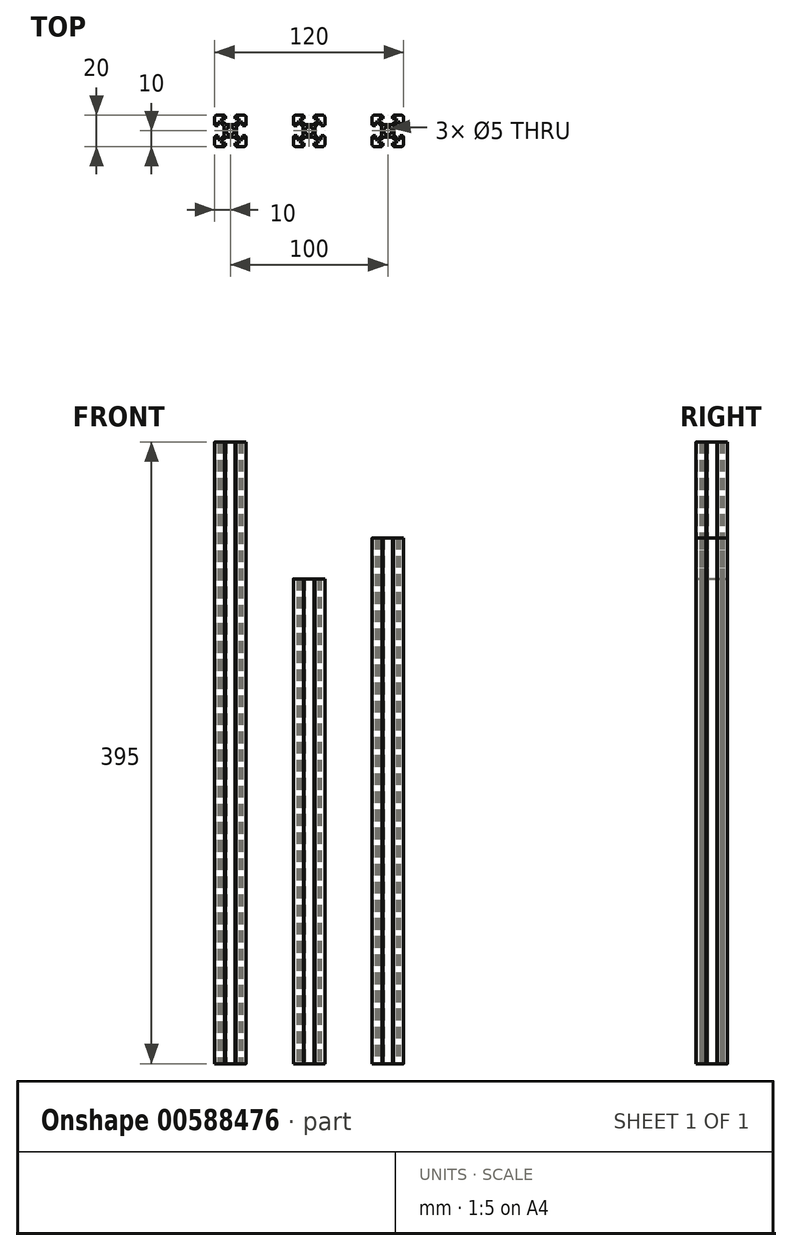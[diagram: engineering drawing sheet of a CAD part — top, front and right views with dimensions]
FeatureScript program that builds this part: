
annotation { "Feature Type Name" : "Feature", "Feature Type Description" : "" }
export const myFeature = defineFeature(function(context is Context, id is Id, definition is map)
    precondition{}
    {
        {
            var Q0;
            Q0=qCreatedBy(makeId("Top.planeOp"),FACE);
            var sketch = newSketch(context, id + "F0", { "sketchPlane" : qUnion([Q0])});
            skLineSegment(sketch, "E0", {"start": v(-2.5, 0) * mm, "end": v(-3.9, 0) * mm});
            skLineSegment(sketch, "E1", {"start": v(-3.9, 0) * mm, "end": v(-3.9, 2.05) * mm});
            skLineSegment(sketch, "E2", {"start": v(-4.49, 3.46) * mm, "end": v(-6.6, 5.58) * mm});
            skLineSegment(sketch, "E3", {"start": v(-6.6, 5.58) * mm, "end": v(-7.7, 5.58) * mm});
            skLineSegment(sketch, "E4", {"start": v(-7.7, 5.58) * mm, "end": v(-7.7, 3.18) * mm});
            skLineSegment(sketch, "E5", {"start": v(-7.7, 3.18) * mm, "end": v(-9.5, 3.18) * mm});
            skLineSegment(sketch, "E6", {"start": v(-9.5, 3.18) * mm, "end": v(-9.5, 3.68) * mm});
            skLineSegment(sketch, "E7", {"start": v(-9.5, 3.68) * mm, "end": v(-10, 3.68) * mm});
            skLineSegment(sketch, "E8", {"start": v(-10, 3.68) * mm, "end": v(-10, 8.5) * mm});
            skLineSegment(sketch, "E9", {"start": v(-8.5, 10) * mm, "end": v(-3.6, 10) * mm});
            skLineSegment(sketch, "E10", {"start": v(-3.6, 10) * mm, "end": v(-3.6, 9.5) * mm});
            skLineSegment(sketch, "E11", {"start": v(-3.6, 9.5) * mm, "end": v(-3.1, 9.5) * mm});
            skLineSegment(sketch, "E12", {"start": v(-3.1, 9.5) * mm, "end": v(-3.1, 7.7) * mm});
            skLineSegment(sketch, "E13", {"start": v(-3.1, 7.7) * mm, "end": v(-5.5, 7.7) * mm});
            skLineSegment(sketch, "E14", {"start": v(-5.5, 7.7) * mm, "end": v(-5.5, 6.6) * mm});
            skLineSegment(sketch, "E15", {"start": v(-5.5, 6.6) * mm, "end": v(-3.39, 4.49) * mm});
            skLineSegment(sketch, "E16", {"start": v(-1.97, 3.9) * mm, "end": v(0, 3.9) * mm});
            skLineSegment(sketch, "E17", {"start": v(0, 3.9) * mm, "end": v(0, 20.22) * mm, "construction": true});
            skLineSegment(sketch, "E18", {"start": v(-3.9, 0) * mm, "end": v(-20.4, 0) * mm, "construction": true});
            skPoint(sketch, "E19.visualSharp", {"position": v(-10, 10) * mm});
            skArc(sketch, "E19.filletArc", {"start": v(-8.5, 10) * mm, "mid": v(-9.56, 9.56) * mm, "end": v(-10, 8.5) * mm});
            skPoint(sketch, "E20.visualSharp", {"position": v(-2.8, 3.9) * mm});
            skArc(sketch, "E20.filletArc", {"start": v(-3.39, 4.49) * mm, "mid": v(-2.74, 4.05) * mm, "end": v(-1.97, 3.9) * mm});
            skPoint(sketch, "E21.visualSharp", {"position": v(-3.9, 2.88) * mm});
            skArc(sketch, "E21.filletArc", {"start": v(-3.9, 2.05) * mm, "mid": v(-4.05, 2.82) * mm, "end": v(-4.49, 3.46) * mm});
            skLineSegment(sketch, "E22", {"start": v(0, 3.9) * mm, "end": v(0, 2.5) * mm});
            skArc(sketch, "E23", {"start": v(-2.5, 0) * mm, "mid": v(-1.77, 1.77) * mm, "end": v(0, 2.5) * mm});
            skLineSegment(sketch, "E24.MirrorCS", {"start": v(9.5, 3.68) * mm, "end": v(10, 3.68) * mm});
            skLineSegment(sketch, "E25.MirrorCS", {"start": v(2.5, 0) * mm, "end": v(3.9, 0) * mm});
            skLineSegment(sketch, "E26.MirrorCS", {"start": v(9.5, 3.18) * mm, "end": v(9.5, 3.68) * mm});
            skArc(sketch, "E27.MirrorCS", {"start": v(3.9, 2.05) * mm, "mid": v(4.05, 2.82) * mm, "end": v(4.49, 3.46) * mm});
            skLineSegment(sketch, "E28.MirrorCS", {"start": v(3.6, 10) * mm, "end": v(3.6, 9.5) * mm});
            skLineSegment(sketch, "E29.MirrorCS", {"start": v(6.6, 5.58) * mm, "end": v(7.7, 5.58) * mm});
            skLineSegment(sketch, "E30.MirrorCS", {"start": v(3.6, 9.5) * mm, "end": v(3.1, 9.5) * mm});
            skLineSegment(sketch, "E31.MirrorCS", {"start": v(5.5, 6.6) * mm, "end": v(3.39, 4.49) * mm});
            skLineSegment(sketch, "E32.MirrorCS", {"start": v(5.5, 7.7) * mm, "end": v(5.5, 6.6) * mm});
            skArc(sketch, "E33.MirrorCS", {"start": v(8.5, 10) * mm, "mid": v(9.56, 9.56) * mm, "end": v(10, 8.5) * mm});
            skLineSegment(sketch, "E34.MirrorCS", {"start": v(3.9, 0) * mm, "end": v(3.9, 2.05) * mm});
            skLineSegment(sketch, "E35.MirrorCS", {"start": v(7.7, 5.58) * mm, "end": v(7.7, 3.18) * mm});
            skLineSegment(sketch, "E36.MirrorCS", {"start": v(7.7, 3.18) * mm, "end": v(9.5, 3.18) * mm});
            skLineSegment(sketch, "E37.MirrorCS", {"start": v(3.1, 7.7) * mm, "end": v(5.5, 7.7) * mm});
            skLineSegment(sketch, "E38.MirrorCS", {"start": v(1.97, 3.9) * mm, "end": v(0, 3.9) * mm});
            skArc(sketch, "E39.MirrorCS", {"start": v(3.39, 4.49) * mm, "mid": v(2.74, 4.05) * mm, "end": v(1.97, 3.9) * mm});
            skLineSegment(sketch, "E40.MirrorCS", {"start": v(3.1, 9.5) * mm, "end": v(3.1, 7.7) * mm});
            skArc(sketch, "E41.MirrorCS", {"start": v(2.5, 0) * mm, "mid": v(1.77, 1.77) * mm, "end": v(0, 2.5) * mm});
            skLineSegment(sketch, "E42.MirrorCS", {"start": v(4.49, 3.46) * mm, "end": v(6.6, 5.58) * mm});
            skLineSegment(sketch, "E43.MirrorCS", {"start": v(8.5, 10) * mm, "end": v(3.6, 10) * mm});
            skPoint(sketch, "E44.MirrorP", {"position": v(3.9, 2.88) * mm});
            skPoint(sketch, "E45.MirrorP", {"position": v(2.8, 3.9) * mm});
            skPoint(sketch, "E46.MirrorP", {"position": v(10, 10) * mm});
            skLineSegment(sketch, "E47.MirrorCS", {"start": v(10, 3.68) * mm, "end": v(10, 8.5) * mm});
            skLineSegment(sketch, "E48.MirrorCS", {"start": v(0, -3.9) * mm, "end": v(0, -2.5) * mm});
            skLineSegment(sketch, "E49.MirrorCS", {"start": v(-9.5, -3.68) * mm, "end": v(-10, -3.68) * mm});
            skLineSegment(sketch, "E50.MirrorCS", {"start": v(-9.5, -3.18) * mm, "end": v(-9.5, -3.68) * mm});
            skLineSegment(sketch, "E51.MirrorCS", {"start": v(-5.5, -7.7) * mm, "end": v(-5.5, -6.6) * mm});
            skLineSegment(sketch, "E52.MirrorCS", {"start": v(3.6, -9.5) * mm, "end": v(3.1, -9.5) * mm});
            skLineSegment(sketch, "E53.MirrorCS", {"start": v(3.6, -10) * mm, "end": v(3.6, -9.5) * mm});
            skLineSegment(sketch, "E54.MirrorCS", {"start": v(-3.9, 0) * mm, "end": v(-3.9, -2.05) * mm});
            skLineSegment(sketch, "E55.MirrorCS", {"start": v(9.5, -3.18) * mm, "end": v(9.5, -3.68) * mm});
            skLineSegment(sketch, "E56.MirrorCS", {"start": v(-5.5, -6.6) * mm, "end": v(-3.39, -4.49) * mm});
            skLineSegment(sketch, "E57.MirrorCS", {"start": v(-6.6, -5.58) * mm, "end": v(-7.7, -5.58) * mm});
            skLineSegment(sketch, "E58.MirrorCS", {"start": v(-4.49, -3.46) * mm, "end": v(-6.6, -5.58) * mm});
            skArc(sketch, "E59.MirrorCS", {"start": v(3.9, -2.05) * mm, "mid": v(4.05, -2.82) * mm, "end": v(4.49, -3.46) * mm});
            skArc(sketch, "E60.MirrorCS", {"start": v(-3.9, -2.05) * mm, "mid": v(-4.05, -2.82) * mm, "end": v(-4.49, -3.46) * mm});
            skLineSegment(sketch, "E61.MirrorCS", {"start": v(3.9, 0) * mm, "end": v(3.9, -2.05) * mm});
            skLineSegment(sketch, "E62.MirrorCS", {"start": v(-3.1, -7.7) * mm, "end": v(-5.5, -7.7) * mm});
            skLineSegment(sketch, "E63.MirrorCS", {"start": v(1.97, -3.9) * mm, "end": v(0, -3.9) * mm});
            skLineSegment(sketch, "E64.MirrorCS", {"start": v(9.5, -3.68) * mm, "end": v(10, -3.68) * mm});
            skLineSegment(sketch, "E65.MirrorCS", {"start": v(7.7, -5.58) * mm, "end": v(7.7, -3.18) * mm});
            skLineSegment(sketch, "E66.MirrorCS", {"start": v(3.1, -9.5) * mm, "end": v(3.1, -7.7) * mm});
            skLineSegment(sketch, "E67.MirrorCS", {"start": v(6.6, -5.58) * mm, "end": v(7.7, -5.58) * mm});
            skLineSegment(sketch, "E68.MirrorCS", {"start": v(7.7, -3.18) * mm, "end": v(9.5, -3.18) * mm});
            skLineSegment(sketch, "E69.MirrorCS", {"start": v(3.1, -7.7) * mm, "end": v(5.5, -7.7) * mm});
            skArc(sketch, "E70.MirrorCS", {"start": v(3.39, -4.49) * mm, "mid": v(2.74, -4.05) * mm, "end": v(1.97, -3.9) * mm});
            skLineSegment(sketch, "E71.MirrorCS", {"start": v(-7.7, -5.58) * mm, "end": v(-7.7, -3.18) * mm});
            skArc(sketch, "E72.MirrorCS", {"start": v(-3.39, -4.49) * mm, "mid": v(-2.74, -4.05) * mm, "end": v(-1.97, -3.9) * mm});
            skLineSegment(sketch, "E73.MirrorCS", {"start": v(-3.1, -9.5) * mm, "end": v(-3.1, -7.7) * mm});
            skLineSegment(sketch, "E74.MirrorCS", {"start": v(5.5, -6.6) * mm, "end": v(3.39, -4.49) * mm});
            skLineSegment(sketch, "E75.MirrorCS", {"start": v(-3.6, -9.5) * mm, "end": v(-3.1, -9.5) * mm});
            skLineSegment(sketch, "E76.MirrorCS", {"start": v(-7.7, -3.18) * mm, "end": v(-9.5, -3.18) * mm});
            skLineSegment(sketch, "E77.MirrorCS", {"start": v(-3.6, -10) * mm, "end": v(-3.6, -9.5) * mm});
            skLineSegment(sketch, "E78.MirrorCS", {"start": v(-1.97, -3.9) * mm, "end": v(0, -3.9) * mm});
            skLineSegment(sketch, "E79.MirrorCS", {"start": v(5.5, -7.7) * mm, "end": v(5.5, -6.6) * mm});
            skArc(sketch, "E80.MirrorCS", {"start": v(8.5, -10) * mm, "mid": v(9.56, -9.56) * mm, "end": v(10, -8.5) * mm});
            skArc(sketch, "E81.MirrorCS", {"start": v(-2.5, 0) * mm, "mid": v(-1.77, -1.77) * mm, "end": v(0, -2.5) * mm});
            skArc(sketch, "E82.MirrorCS", {"start": v(-8.5, -10) * mm, "mid": v(-9.56, -9.56) * mm, "end": v(-10, -8.5) * mm});
            skLineSegment(sketch, "E83.MirrorCS", {"start": v(-8.5, -10) * mm, "end": v(-3.6, -10) * mm});
            skLineSegment(sketch, "E84.MirrorCS", {"start": v(8.5, -10) * mm, "end": v(3.6, -10) * mm});
            skLineSegment(sketch, "E85.MirrorCS", {"start": v(0, -3.9) * mm, "end": v(0, -20.22) * mm, "construction": true});
            skLineSegment(sketch, "E86.MirrorCS", {"start": v(10, -3.68) * mm, "end": v(10, -8.5) * mm});
            skLineSegment(sketch, "E87.MirrorCS", {"start": v(-10, -3.68) * mm, "end": v(-10, -8.5) * mm});
            skLineSegment(sketch, "E88.MirrorCS", {"start": v(4.49, -3.46) * mm, "end": v(6.6, -5.58) * mm});
            skPoint(sketch, "E89.MirrorP", {"position": v(10, -10) * mm});
            skPoint(sketch, "E90.MirrorP", {"position": v(-3.9, -2.88) * mm});
            skArc(sketch, "E91.MirrorCS", {"start": v(2.5, 0) * mm, "mid": v(1.77, -1.77) * mm, "end": v(0, -2.5) * mm});
            skPoint(sketch, "E92.MirrorP", {"position": v(-2.8, -3.9) * mm});
            skPoint(sketch, "E93.MirrorP", {"position": v(-10, -10) * mm});
            skPoint(sketch, "E94.MirrorP", {"position": v(3.9, -2.88) * mm});
            skPoint(sketch, "E95.MirrorP", {"position": v(2.8, -3.9) * mm});
            skSolve(sketch);
        }
        {
            var Q0;
            Q0 = qSketchRegion(id + "F0", true);
            extrude(context, id + "F1", {"entities" : qUnion([Q0]), "depth" : 334 * mm, "offsetDistance" : 25 * mm});
        }
        {
            var Q0;
            Q0=makeQuery(id+"F1.opExtrude","SWEPT_BODY",BODY,{"disambiguationData":[OSD([sQuery(id+"F0.wireOp",EDGE,"E1"),sQuery(id+"F0.wireOp",EDGE,"E2"),sQuery(id+"F0.wireOp",EDGE,"E3"),sQuery(id+"F0.wireOp",EDGE,"E4"),sQuery(id+"F0.wireOp",EDGE,"E5"),sQuery(id+"F0.wireOp",EDGE,"E6"),sQuery(id+"F0.wireOp",EDGE,"E7"),sQuery(id+"F0.wireOp",EDGE,"E8"),sQuery(id+"F0.wireOp",EDGE,"E9"),sQuery(id+"F0.wireOp",EDGE,"E10"),sQuery(id+"F0.wireOp",EDGE,"E11"),sQuery(id+"F0.wireOp",EDGE,"E12"),sQuery(id+"F0.wireOp",EDGE,"E13"),sQuery(id+"F0.wireOp",EDGE,"E14"),sQuery(id+"F0.wireOp",EDGE,"E15"),sQuery(id+"F0.wireOp",EDGE,"E16"),sQuery(id+"F0.wireOp",EDGE,"E19.filletArc"),sQuery(id+"F0.wireOp",EDGE,"E20.filletArc"),sQuery(id+"F0.wireOp",EDGE,"E21.filletArc"),sQuery(id+"F0.wireOp",EDGE,"E23"),sQuery(id+"F0.wireOp",EDGE,"E24.MirrorCS"),sQuery(id+"F0.wireOp",EDGE,"E26.MirrorCS"),sQuery(id+"F0.wireOp",EDGE,"E27.MirrorCS"),sQuery(id+"F0.wireOp",EDGE,"E28.MirrorCS"),sQuery(id+"F0.wireOp",EDGE,"E29.MirrorCS"),sQuery(id+"F0.wireOp",EDGE,"E30.MirrorCS"),sQuery(id+"F0.wireOp",EDGE,"E31.MirrorCS"),sQuery(id+"F0.wireOp",EDGE,"E32.MirrorCS"),sQuery(id+"F0.wireOp",EDGE,"E33.MirrorCS"),sQuery(id+"F0.wireOp",EDGE,"E34.MirrorCS"),sQuery(id+"F0.wireOp",EDGE,"E35.MirrorCS"),sQuery(id+"F0.wireOp",EDGE,"E36.MirrorCS"),sQuery(id+"F0.wireOp",EDGE,"E37.MirrorCS"),sQuery(id+"F0.wireOp",EDGE,"E38.MirrorCS"),sQuery(id+"F0.wireOp",EDGE,"E39.MirrorCS"),sQuery(id+"F0.wireOp",EDGE,"E40.MirrorCS"),sQuery(id+"F0.wireOp",EDGE,"E41.MirrorCS"),sQuery(id+"F0.wireOp",EDGE,"E42.MirrorCS"),sQuery(id+"F0.wireOp",EDGE,"E43.MirrorCS"),sQuery(id+"F0.wireOp",EDGE,"E47.MirrorCS"),sQuery(id+"F0.wireOp",EDGE,"E49.MirrorCS"),sQuery(id+"F0.wireOp",EDGE,"E50.MirrorCS"),sQuery(id+"F0.wireOp",EDGE,"E51.MirrorCS"),sQuery(id+"F0.wireOp",EDGE,"E52.MirrorCS"),sQuery(id+"F0.wireOp",EDGE,"E53.MirrorCS"),sQuery(id+"F0.wireOp",EDGE,"E54.MirrorCS"),sQuery(id+"F0.wireOp",EDGE,"E55.MirrorCS"),sQuery(id+"F0.wireOp",EDGE,"E56.MirrorCS"),sQuery(id+"F0.wireOp",EDGE,"E57.MirrorCS"),sQuery(id+"F0.wireOp",EDGE,"E58.MirrorCS"),sQuery(id+"F0.wireOp",EDGE,"E59.MirrorCS"),sQuery(id+"F0.wireOp",EDGE,"E60.MirrorCS"),sQuery(id+"F0.wireOp",EDGE,"E61.MirrorCS"),sQuery(id+"F0.wireOp",EDGE,"E62.MirrorCS"),sQuery(id+"F0.wireOp",EDGE,"E63.MirrorCS"),sQuery(id+"F0.wireOp",EDGE,"E64.MirrorCS"),sQuery(id+"F0.wireOp",EDGE,"E65.MirrorCS"),sQuery(id+"F0.wireOp",EDGE,"E66.MirrorCS"),sQuery(id+"F0.wireOp",EDGE,"E67.MirrorCS"),sQuery(id+"F0.wireOp",EDGE,"E68.MirrorCS"),sQuery(id+"F0.wireOp",EDGE,"E69.MirrorCS"),sQuery(id+"F0.wireOp",EDGE,"E70.MirrorCS"),sQuery(id+"F0.wireOp",EDGE,"E71.MirrorCS"),sQuery(id+"F0.wireOp",EDGE,"E72.MirrorCS"),sQuery(id+"F0.wireOp",EDGE,"E73.MirrorCS"),sQuery(id+"F0.wireOp",EDGE,"E74.MirrorCS"),sQuery(id+"F0.wireOp",EDGE,"E75.MirrorCS"),sQuery(id+"F0.wireOp",EDGE,"E76.MirrorCS"),sQuery(id+"F0.wireOp",EDGE,"E77.MirrorCS"),sQuery(id+"F0.wireOp",EDGE,"E78.MirrorCS"),sQuery(id+"F0.wireOp",EDGE,"E79.MirrorCS"),sQuery(id+"F0.wireOp",EDGE,"E80.MirrorCS"),sQuery(id+"F0.wireOp",EDGE,"E81.MirrorCS"),sQuery(id+"F0.wireOp",EDGE,"E82.MirrorCS"),sQuery(id+"F0.wireOp",EDGE,"E83.MirrorCS"),sQuery(id+"F0.wireOp",EDGE,"E84.MirrorCS"),sQuery(id+"F0.wireOp",EDGE,"E86.MirrorCS"),sQuery(id+"F0.wireOp",EDGE,"E87.MirrorCS"),sQuery(id+"F0.wireOp",EDGE,"E88.MirrorCS"),sQuery(id+"F0.wireOp",EDGE,"E91.MirrorCS")])]});
            transform(context, id + "F2", {"entities" : qUnion([Q0]), "transformType" : TransformType.TRANSLATION_3D, "dx" : 100 * mm, "dy" : 0 * mm, "dz" : 0 * mm, "makeCopy" : false});
        }
        {
            var Q0;
            Q0=makeQuery(id+"F0.imprint","IMPRINT",FACE,{"disambiguationData":[TD([[makeQuery(id+"F0.imprint","IMPRINT",EDGE,{"derivedFrom":sQuery(id+"F0.wireOp",EDGE,"E48.MirrorCS")}),1.0]])]});
            var Q1;
            Q1=makeQuery(id+"F0.imprint","IMPRINT",FACE,{"disambiguationData":[TD([[makeQuery(id+"F0.imprint","IMPRINT",EDGE,{"derivedFrom":sQuery(id+"F0.wireOp",EDGE,"E1")}),-1.0]])]});
            var Q2;
            Q2=makeQuery(id+"F0.imprint","IMPRINT",FACE,{"disambiguationData":[TD([[makeQuery(id+"F0.imprint","IMPRINT",EDGE,{"derivedFrom":sQuery(id+"F0.wireOp",EDGE,"E24.MirrorCS")}),1.0]])]});
            var Q3;
            Q3=makeQuery(id+"F0.imprint","IMPRINT",FACE,{"disambiguationData":[TD([[makeQuery(id+"F0.imprint","IMPRINT",EDGE,{"derivedFrom":sQuery(id+"F0.wireOp",EDGE,"E48.MirrorCS")}),-1.0]])]});
            extrude(context, id + "F3", {"entities" : qUnion([Q0, Q1, Q2, Q3]), "depth" : 308 * mm, "offsetDistance" : 25 * mm});
        }
        {
            var Q0;
            Q0=makeQuery(id+"F3.opExtrude","SWEPT_BODY",BODY,{"disambiguationData":[OSD([sQuery(id+"F0.wireOp",EDGE,"E1"),sQuery(id+"F0.wireOp",EDGE,"E2"),sQuery(id+"F0.wireOp",EDGE,"E3"),sQuery(id+"F0.wireOp",EDGE,"E4"),sQuery(id+"F0.wireOp",EDGE,"E5"),sQuery(id+"F0.wireOp",EDGE,"E6"),sQuery(id+"F0.wireOp",EDGE,"E7"),sQuery(id+"F0.wireOp",EDGE,"E8"),sQuery(id+"F0.wireOp",EDGE,"E9"),sQuery(id+"F0.wireOp",EDGE,"E10"),sQuery(id+"F0.wireOp",EDGE,"E11"),sQuery(id+"F0.wireOp",EDGE,"E12"),sQuery(id+"F0.wireOp",EDGE,"E13"),sQuery(id+"F0.wireOp",EDGE,"E14"),sQuery(id+"F0.wireOp",EDGE,"E15"),sQuery(id+"F0.wireOp",EDGE,"E16"),sQuery(id+"F0.wireOp",EDGE,"E19.filletArc"),sQuery(id+"F0.wireOp",EDGE,"E20.filletArc"),sQuery(id+"F0.wireOp",EDGE,"E21.filletArc"),sQuery(id+"F0.wireOp",EDGE,"E23"),sQuery(id+"F0.wireOp",EDGE,"E24.MirrorCS"),sQuery(id+"F0.wireOp",EDGE,"E26.MirrorCS"),sQuery(id+"F0.wireOp",EDGE,"E27.MirrorCS"),sQuery(id+"F0.wireOp",EDGE,"E28.MirrorCS"),sQuery(id+"F0.wireOp",EDGE,"E29.MirrorCS"),sQuery(id+"F0.wireOp",EDGE,"E30.MirrorCS"),sQuery(id+"F0.wireOp",EDGE,"E31.MirrorCS"),sQuery(id+"F0.wireOp",EDGE,"E32.MirrorCS"),sQuery(id+"F0.wireOp",EDGE,"E33.MirrorCS"),sQuery(id+"F0.wireOp",EDGE,"E34.MirrorCS"),sQuery(id+"F0.wireOp",EDGE,"E35.MirrorCS"),sQuery(id+"F0.wireOp",EDGE,"E36.MirrorCS"),sQuery(id+"F0.wireOp",EDGE,"E37.MirrorCS"),sQuery(id+"F0.wireOp",EDGE,"E38.MirrorCS"),sQuery(id+"F0.wireOp",EDGE,"E39.MirrorCS"),sQuery(id+"F0.wireOp",EDGE,"E40.MirrorCS"),sQuery(id+"F0.wireOp",EDGE,"E41.MirrorCS"),sQuery(id+"F0.wireOp",EDGE,"E42.MirrorCS"),sQuery(id+"F0.wireOp",EDGE,"E43.MirrorCS"),sQuery(id+"F0.wireOp",EDGE,"E47.MirrorCS"),sQuery(id+"F0.wireOp",EDGE,"E49.MirrorCS"),sQuery(id+"F0.wireOp",EDGE,"E50.MirrorCS"),sQuery(id+"F0.wireOp",EDGE,"E51.MirrorCS"),sQuery(id+"F0.wireOp",EDGE,"E52.MirrorCS"),sQuery(id+"F0.wireOp",EDGE,"E53.MirrorCS"),sQuery(id+"F0.wireOp",EDGE,"E54.MirrorCS"),sQuery(id+"F0.wireOp",EDGE,"E55.MirrorCS"),sQuery(id+"F0.wireOp",EDGE,"E56.MirrorCS"),sQuery(id+"F0.wireOp",EDGE,"E57.MirrorCS"),sQuery(id+"F0.wireOp",EDGE,"E58.MirrorCS"),sQuery(id+"F0.wireOp",EDGE,"E59.MirrorCS"),sQuery(id+"F0.wireOp",EDGE,"E60.MirrorCS"),sQuery(id+"F0.wireOp",EDGE,"E61.MirrorCS"),sQuery(id+"F0.wireOp",EDGE,"E62.MirrorCS"),sQuery(id+"F0.wireOp",EDGE,"E63.MirrorCS"),sQuery(id+"F0.wireOp",EDGE,"E64.MirrorCS"),sQuery(id+"F0.wireOp",EDGE,"E65.MirrorCS"),sQuery(id+"F0.wireOp",EDGE,"E66.MirrorCS"),sQuery(id+"F0.wireOp",EDGE,"E67.MirrorCS"),sQuery(id+"F0.wireOp",EDGE,"E68.MirrorCS"),sQuery(id+"F0.wireOp",EDGE,"E69.MirrorCS"),sQuery(id+"F0.wireOp",EDGE,"E70.MirrorCS"),sQuery(id+"F0.wireOp",EDGE,"E71.MirrorCS"),sQuery(id+"F0.wireOp",EDGE,"E72.MirrorCS"),sQuery(id+"F0.wireOp",EDGE,"E73.MirrorCS"),sQuery(id+"F0.wireOp",EDGE,"E74.MirrorCS"),sQuery(id+"F0.wireOp",EDGE,"E75.MirrorCS"),sQuery(id+"F0.wireOp",EDGE,"E76.MirrorCS"),sQuery(id+"F0.wireOp",EDGE,"E77.MirrorCS"),sQuery(id+"F0.wireOp",EDGE,"E78.MirrorCS"),sQuery(id+"F0.wireOp",EDGE,"E79.MirrorCS"),sQuery(id+"F0.wireOp",EDGE,"E80.MirrorCS"),sQuery(id+"F0.wireOp",EDGE,"E81.MirrorCS"),sQuery(id+"F0.wireOp",EDGE,"E82.MirrorCS"),sQuery(id+"F0.wireOp",EDGE,"E83.MirrorCS"),sQuery(id+"F0.wireOp",EDGE,"E84.MirrorCS"),sQuery(id+"F0.wireOp",EDGE,"E86.MirrorCS"),sQuery(id+"F0.wireOp",EDGE,"E87.MirrorCS"),sQuery(id+"F0.wireOp",EDGE,"E88.MirrorCS"),sQuery(id+"F0.wireOp",EDGE,"E91.MirrorCS")])]});
            transform(context, id + "F4", {"entities" : qUnion([Q0]), "transformType" : TransformType.TRANSLATION_3D, "dx" : 50 * mm, "dy" : 0 * mm, "dz" : 0 * mm, "makeCopy" : false});
        }
        {
            var Q0;
            Q0=makeQuery(id+"F0.imprint","IMPRINT",FACE,{"disambiguationData":[TD([[makeQuery(id+"F0.imprint","IMPRINT",EDGE,{"derivedFrom":sQuery(id+"F0.wireOp",EDGE,"E48.MirrorCS")}),1.0]])]});
            var Q1;
            Q1=makeQuery(id+"F0.imprint","IMPRINT",FACE,{"disambiguationData":[TD([[makeQuery(id+"F0.imprint","IMPRINT",EDGE,{"derivedFrom":sQuery(id+"F0.wireOp",EDGE,"E1")}),-1.0]])]});
            var Q2;
            Q2=makeQuery(id+"F0.imprint","IMPRINT",FACE,{"disambiguationData":[TD([[makeQuery(id+"F0.imprint","IMPRINT",EDGE,{"derivedFrom":sQuery(id+"F0.wireOp",EDGE,"E24.MirrorCS")}),1.0]])]});
            var Q3;
            Q3=makeQuery(id+"F0.imprint","IMPRINT",FACE,{"disambiguationData":[TD([[makeQuery(id+"F0.imprint","IMPRINT",EDGE,{"derivedFrom":sQuery(id+"F0.wireOp",EDGE,"E48.MirrorCS")}),-1.0]])]});
            extrude(context, id + "F5", {"entities" : qUnion([Q0, Q1, Q2, Q3]), "depth" : 395 * mm, "offsetDistance" : 25 * mm});
        }
    });
